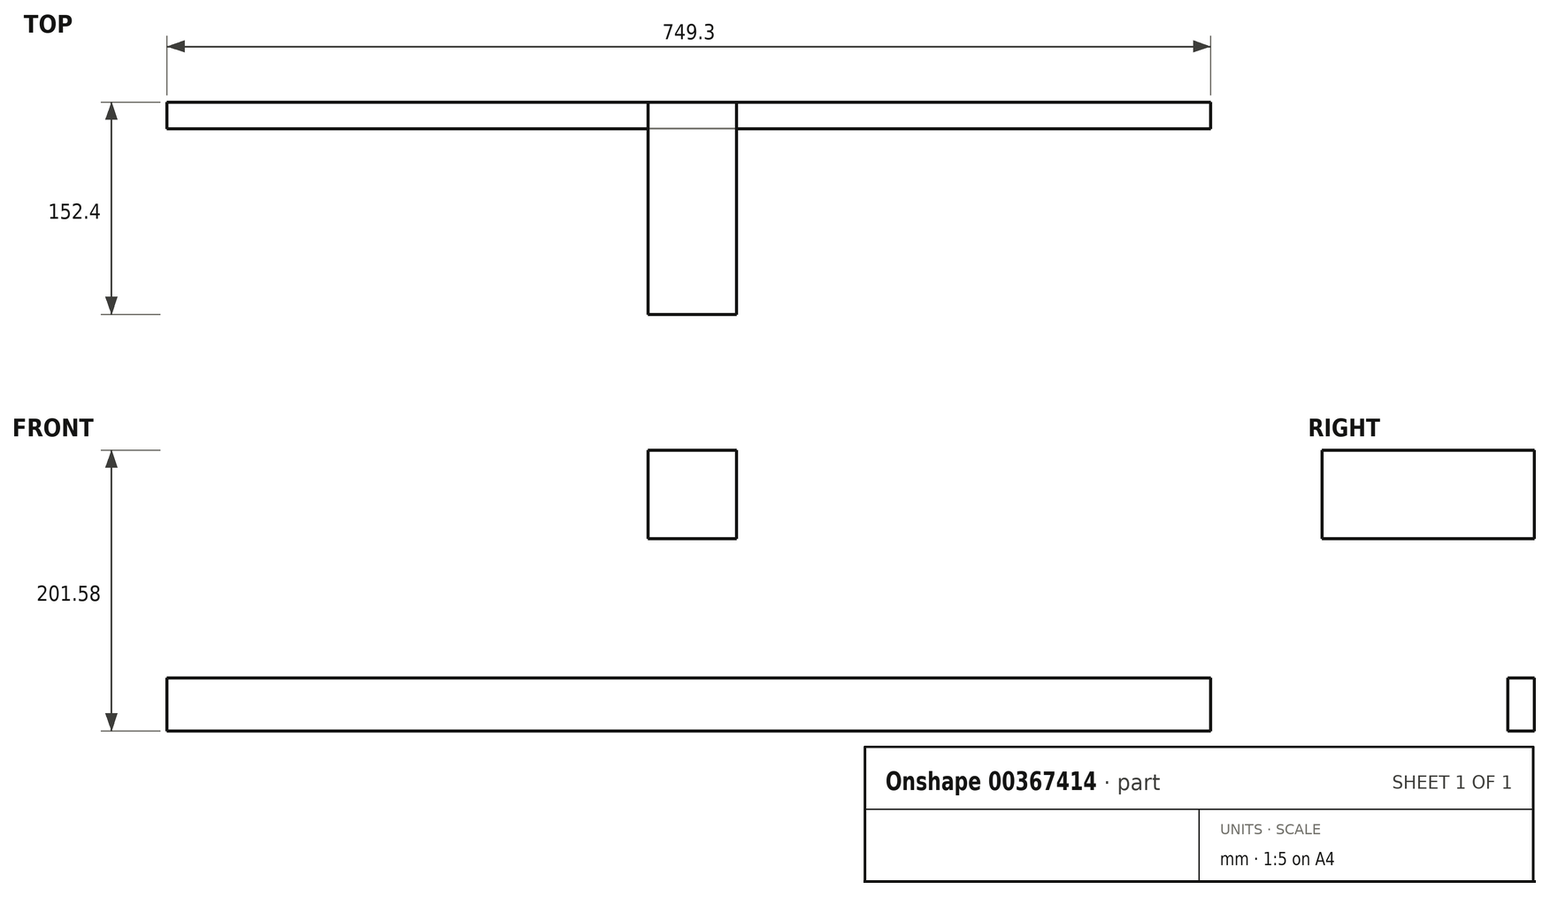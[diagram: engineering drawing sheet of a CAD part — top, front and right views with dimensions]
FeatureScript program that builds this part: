
annotation { "Feature Type Name" : "Feature", "Feature Type Description" : "" }
export const myFeature = defineFeature(function(context is Context, id is Id, definition is map)
    precondition{}
    {
        {
            var Q0;
            Q0=qCreatedBy(makeId("Front.planeOp"),FACE);
            var sketch = newSketch(context, id + "F0", { "sketchPlane" : qUnion([Q0])});
            skLineSegment(sketch, "E0.bottom", {"start": v(374.65, 19.05) * mm, "end": v(-374.65, 19.05) * mm});
            skLineSegment(sketch, "E0.top", {"start": v(374.65, -19.05) * mm, "end": v(-374.65, -19.05) * mm});
            skLineSegment(sketch, "E0.left", {"start": v(374.65, 19.05) * mm, "end": v(374.65, -19.05) * mm});
            skLineSegment(sketch, "E0.right", {"start": v(-374.65, 19.05) * mm, "end": v(-374.65, -19.05) * mm});
            skPoint(sketch, "E0.middle", {"position": v(0, 0) * mm});
            skSolve(sketch);
        }
        {
            var Q0;
            Q0 = qSketchRegion(id + "F0", true);
            extrude(context, id + "F1", {"entities" : qUnion([Q0]), "depth" : 19.05 * mm});
        }
        {
            var Q0;
            Q0=qCreatedBy(makeId("Front.planeOp"),FACE);
            var sketch = newSketch(context, id + "F2", { "sketchPlane" : qUnion([Q0])});
            skLineSegment(sketch, "E1.bottom", {"start": v(34.08, 182.53) * mm, "end": v(-29.42, 182.53) * mm});
            skLineSegment(sketch, "E1.top", {"start": v(34.08, 119.03) * mm, "end": v(-29.42, 119.03) * mm});
            skLineSegment(sketch, "E1.left", {"start": v(34.08, 182.53) * mm, "end": v(34.08, 119.03) * mm});
            skLineSegment(sketch, "E1.right", {"start": v(-29.42, 182.53) * mm, "end": v(-29.42, 119.03) * mm});
            skPoint(sketch, "E1.middle", {"position": v(2.33, 150.78) * mm});
            skSolve(sketch);
        }
        {
            var Q0;
            Q0 = qSketchRegion(id + "F2", true);
            extrude(context, id + "F3", {"entities" : qUnion([Q0]), "depth" : 152.4 * mm});
        }
    });
